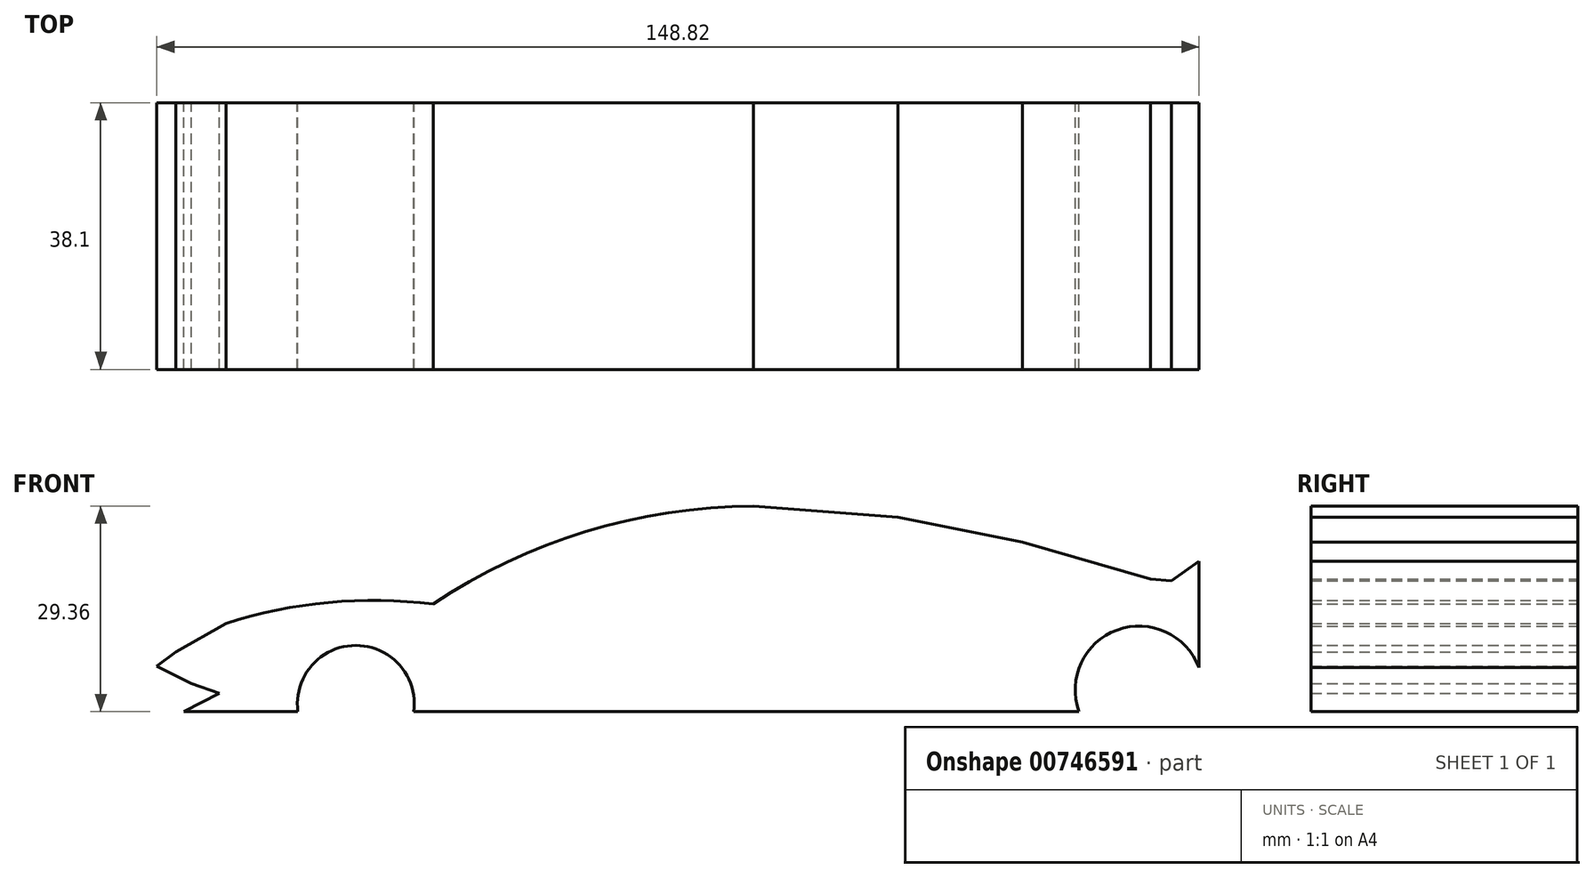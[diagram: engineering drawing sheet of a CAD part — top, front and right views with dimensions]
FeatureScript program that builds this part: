
annotation { "Feature Type Name" : "Feature", "Feature Type Description" : "" }
export const myFeature = defineFeature(function(context is Context, id is Id, definition is map)
    precondition{}
    {
        {
            var Q0;
            Q0=qCreatedBy(makeId("Front.planeOp"),FACE);
            var sketch = newSketch(context, id + "F0", { "sketchPlane" : qUnion([Q0])});
            skArc(sketch, "E0", {"start": v(3.05, 25.32) * mm, "mid": v(-20.83, 21.67) * mm, "end": v(-42.67, 11.33) * mm});
            skArc(sketch, "E1", {"start": v(-42.67, 11.33) * mm, "mid": v(-57.6, 11.55) * mm, "end": v(-72.23, 8.57) * mm});
            skLineSegment(sketch, "E2", {"start": v(3.05, 25.32) * mm, "end": v(23.75, 23.75) * mm});
            skLineSegment(sketch, "E3", {"start": v(23.75, 23.75) * mm, "end": v(41.48, 20.2) * mm});
            skLineSegment(sketch, "E4", {"start": v(41.48, 20.2) * mm, "end": v(59.81, 14.88) * mm});
            skLineSegment(sketch, "E5", {"start": v(59.81, 14.88) * mm, "end": v(62.78, 14.65) * mm});
            skLineSegment(sketch, "E6", {"start": v(62.78, 14.65) * mm, "end": v(66.7, 17.44) * mm});
            skLineSegment(sketch, "E7", {"start": v(66.7, 17.44) * mm, "end": v(66.7, 6.2) * mm});
            skLineSegment(sketch, "E8", {"start": v(66.7, 6.2) * mm, "end": v(66.7, 2.27) * mm});
            skArc(sketch, "E9", {"start": v(66.7, 2.27) * mm, "mid": v(55, 7.62) * mm, "end": v(49.56, -4.04) * mm});
            skLineSegment(sketch, "E10", {"start": v(49.56, -4.04) * mm, "end": v(-45.42, -4.04) * mm});
            skArc(sketch, "E11", {"start": v(-45.42, -4.04) * mm, "mid": v(-53.7, 5.42) * mm, "end": v(-61.98, -4.04) * mm});
            skLineSegment(sketch, "E12", {"start": v(-61.98, -4.04) * mm, "end": v(-67.5, -4.04) * mm});
            skLineSegment(sketch, "E13", {"start": v(-67.5, -4.04) * mm, "end": v(-78.3, -4.04) * mm});
            skLineSegment(sketch, "E14", {"start": v(-78.3, -4.04) * mm, "end": v(-73.2, -1.4) * mm});
            skLineSegment(sketch, "E15", {"start": v(-73.2, -1.4) * mm, "end": v(-77.17, 0) * mm});
            skLineSegment(sketch, "E16", {"start": v(-72.23, 8.57) * mm, "end": v(-79.4, 4.49) * mm});
            skLineSegment(sketch, "E17", {"start": v(-79.4, 4.49) * mm, "end": v(-82.1, 2.46) * mm});
            skLineSegment(sketch, "E18", {"start": v(-82.1, 2.46) * mm, "end": v(-77.17, 0) * mm});
            skSolve(sketch);
        }
        {
            var Q0;
            Q0 = qSketchRegion(id + "F0", true);
            extrude(context, id + "F1", {"entities" : qUnion([Q0]), "depth" : 38.1 * mm, "offsetDistance" : 25.4 * mm});
        }
    });
